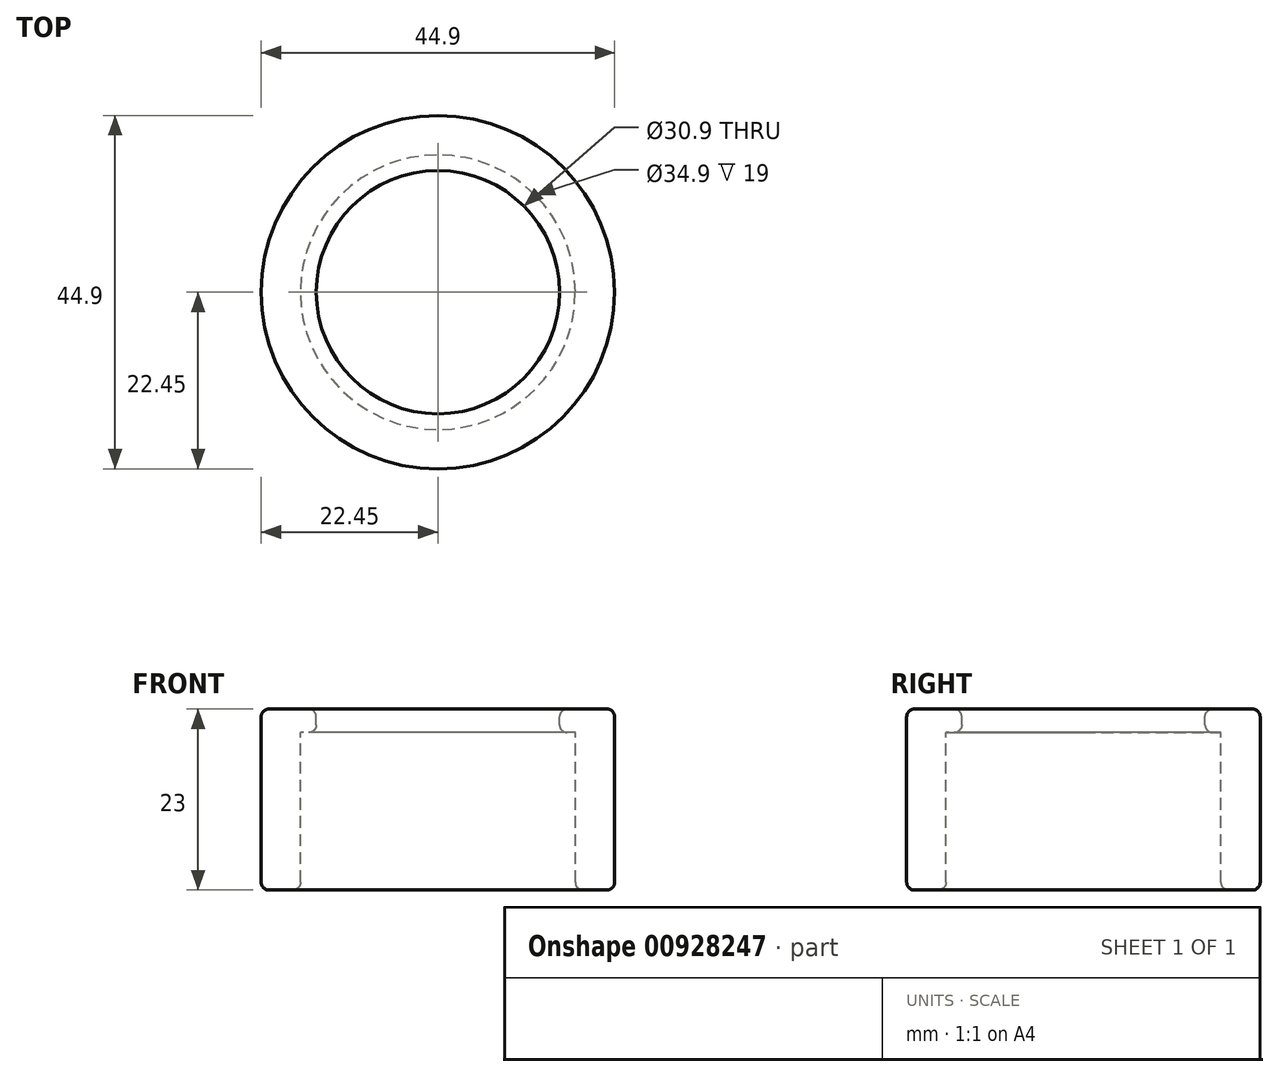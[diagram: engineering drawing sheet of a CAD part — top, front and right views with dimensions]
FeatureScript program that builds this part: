
annotation { "Feature Type Name" : "Feature", "Feature Type Description" : "" }
export const myFeature = defineFeature(function(context is Context, id is Id, definition is map)
    precondition{}
    {
        {
            var Q0;
            Q0=qCreatedBy(makeId("Right.planeOp"),FACE);
            var sketch = newSketch(context, id + "F0", { "sketchPlane" : qUnion([Q0])});
            skLineSegment(sketch, "E0", {"start": v(0, 15.65) * mm, "end": v(0, -22.16) * mm, "construction": true});
            skLineSegment(sketch, "E1", {"start": v(16.45, 3) * mm, "end": v(21.45, 3) * mm});
            skLineSegment(sketch, "E2", {"start": v(22.45, 2) * mm, "end": v(22.45, -19) * mm});
            skLineSegment(sketch, "E3", {"start": v(21.45, -20) * mm, "end": v(18.45, -20) * mm});
            skLineSegment(sketch, "E4", {"start": v(17.45, -19) * mm, "end": v(17.45, 0) * mm});
            skLineSegment(sketch, "E5", {"start": v(17.45, 0) * mm, "end": v(16.45, 0) * mm});
            skLineSegment(sketch, "E6", {"start": v(15.45, 1) * mm, "end": v(15.45, 2) * mm});
            skPoint(sketch, "E7.visualSharp", {"position": v(15.45, 3) * mm});
            skArc(sketch, "E7.filletArc", {"start": v(16.45, 3) * mm, "mid": v(15.74, 2.7) * mm, "end": v(15.45, 2) * mm});
            skPoint(sketch, "E8.visualSharp", {"position": v(15.45, 0) * mm});
            skArc(sketch, "E8.filletArc", {"start": v(15.45, 1) * mm, "mid": v(15.74, 0.3) * mm, "end": v(16.45, 0) * mm});
            skPoint(sketch, "E9.visualSharp", {"position": v(22.45, 3) * mm});
            skArc(sketch, "E9.filletArc", {"start": v(22.45, 2) * mm, "mid": v(22.16, 2.7) * mm, "end": v(21.45, 3) * mm});
            skPoint(sketch, "E10.visualSharp", {"position": v(22.45, -20) * mm});
            skArc(sketch, "E10.filletArc", {"start": v(21.45, -20) * mm, "mid": v(22.16, -19.7) * mm, "end": v(22.45, -19) * mm});
            skPoint(sketch, "E11.visualSharp", {"position": v(17.45, -20) * mm});
            skArc(sketch, "E11.filletArc", {"start": v(17.45, -19) * mm, "mid": v(17.74, -19.7) * mm, "end": v(18.45, -20) * mm});
            skSolve(sketch);
        }
        {
            var Q0;
            Q0=makeQuery(id+"F0.imprint","IMPRINT",FACE,{"disambiguationData":[TD([[makeQuery(id+"F0.imprint","IMPRINT",EDGE,{"derivedFrom":sQuery(id+"F0.wireOp",EDGE,"E1")}),-1.0]])]});
            var Q1;
            Q1=qConstructionFilter(qBodyType(qCreatedBy(id+"F0",EDGE),BodyType.WIRE),ConstructionObject.NO);
            var Q2;
            Q2=sQuery(id+"F0.wireOp",EDGE,"E0");
            revolve(context, id + "F1", {"surfaceOperationType" : NewSurfaceOperationType.NEW, "entities" : qUnion([Q0]), "surfaceEntities" : qUnion([Q1]), "axis" : qUnion([Q2]), "revolveType" : RevolveType.FULL});
        }
    });
